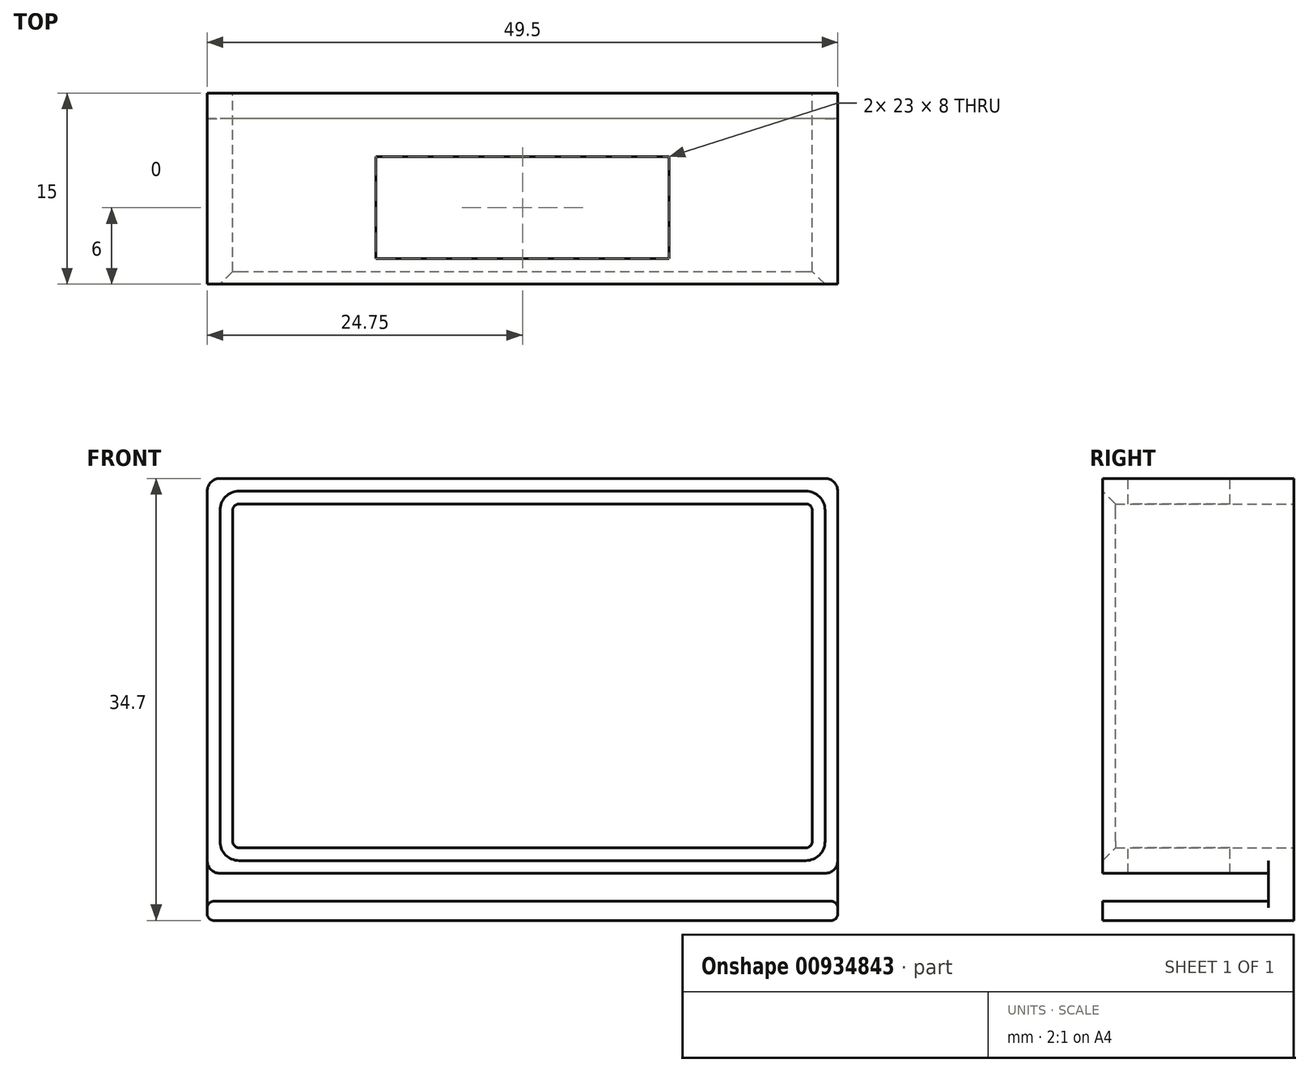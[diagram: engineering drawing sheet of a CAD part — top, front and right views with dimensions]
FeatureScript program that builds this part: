
annotation { "Feature Type Name" : "Feature", "Feature Type Description" : "" }
export const myFeature = defineFeature(function(context is Context, id is Id, definition is map)
    precondition{}
    {
        {
            var Q0;
            Q0=qCreatedBy(makeId("Front.planeOp"),FACE);
            var sketch = newSketch(context, id + "F0", { "sketchPlane" : qUnion([Q0])});
            skLineSegment(sketch, "E0.bottom", {"start": v(22.75, -13.5) * mm, "end": v(-22.75, -13.5) * mm});
            skLineSegment(sketch, "E0.top", {"start": v(22.75, 13.5) * mm, "end": v(-22.75, 13.5) * mm});
            skLineSegment(sketch, "E0.left", {"start": v(22.75, -13.5) * mm, "end": v(22.75, 13.5) * mm});
            skLineSegment(sketch, "E0.right", {"start": v(-22.75, -13.5) * mm, "end": v(-22.75, 13.5) * mm});
            skPoint(sketch, "E0.middle", {"position": v(0, 0) * mm});
            skLineSegment(sketch, "E1.bottom", {"start": v(24.75, -15.5) * mm, "end": v(-24.75, -15.5) * mm});
            skLineSegment(sketch, "E1.top", {"start": v(24.75, 15.5) * mm, "end": v(-24.75, 15.5) * mm});
            skLineSegment(sketch, "E1.left", {"start": v(24.75, -15.5) * mm, "end": v(24.75, 15.5) * mm});
            skLineSegment(sketch, "E1.right", {"start": v(-24.75, -15.5) * mm, "end": v(-24.75, 15.5) * mm});
            skLineSegment(sketch, "E2", {"start": v(22.75, -13.5) * mm, "end": v(22.75, -15.5) * mm, "construction": true});
            skLineSegment(sketch, "E3", {"start": v(22.75, -13.5) * mm, "end": v(24.75, -13.5) * mm, "construction": true});
            skSolve(sketch);
        }
        {
            var Q0;
            Q0 = qSketchRegion(id + "F0", true);
            extrude(context, id + "F1", {"entities" : qUnion([Q0]), "depth" : 15 * mm, "offsetDistance" : 25 * mm});
        }
        {
            var Q0;
            Q0=makeQuery(id+"F1.opExtrude","SWEPT_FACE",FACE,{"disambiguationData":[OSD([sQuery(id+"F0.wireOp",EDGE,"E1.top")])]});
            var sketch = newSketch(context, id + "F2", { "sketchPlane" : qUnion([Q0])});
            skLineSegment(sketch, "E4.bottom", {"start": v(11.5, -13) * mm, "end": v(-11.5, -13) * mm});
            skLineSegment(sketch, "E4.top", {"start": v(11.5, -5) * mm, "end": v(-11.5, -5) * mm});
            skLineSegment(sketch, "E4.left", {"start": v(11.5, -13) * mm, "end": v(11.5, -5) * mm});
            skLineSegment(sketch, "E4.right", {"start": v(-11.5, -13) * mm, "end": v(-11.5, -5) * mm});
            skPoint(sketch, "E4.middle", {"position": v(0, -9) * mm});
            skSolve(sketch);
        }
        {
            var Q0;
            Q0 = qSketchRegion(id + "F2", true);
            extrude(context, id + "F3", {"entities" : qUnion([Q0]), "operationType" : NewBodyOperationType.REMOVE, "endBound" : BoundingType.THROUGH_ALL, "oppositeDirection" : true, "depth" : 25 * mm, "offsetDistance" : 25 * mm});
        }
        {
            var Q0;
            Q0=makeQuery(id+"F1.opExtrude","SWEPT_EDGE",EDGE,{"disambiguationData":[OSD([sQuery(id+"F0.wireOp",EDGE,"E1.top"),sQuery(id+"F0.wireOp",EDGE,"E1.left")])]});
            var Q1;
            Q1=makeQuery(id+"F1.opExtrude","SWEPT_EDGE",EDGE,{"disambiguationData":[OSD([sQuery(id+"F0.wireOp",EDGE,"E1.bottom"),sQuery(id+"F0.wireOp",EDGE,"E1.left")])]});
            var Q2;
            Q2=makeQuery(id+"F1.opExtrude","SWEPT_EDGE",EDGE,{"disambiguationData":[OSD([sQuery(id+"F0.wireOp",EDGE,"E1.top"),sQuery(id+"F0.wireOp",EDGE,"E1.right")])]});
            var Q3;
            Q3=makeQuery(id+"F1.opExtrude","SWEPT_EDGE",EDGE,{"disambiguationData":[OSD([sQuery(id+"F0.wireOp",EDGE,"E1.bottom"),sQuery(id+"F0.wireOp",EDGE,"E1.right")])]});
            fillet(context, id + "F4", {"entities" : qUnion([Q0, Q1, Q2, Q3]), "radius" : 1 * mm, "tangentPropagation" : true, "allowEdgeOverflow" : false});
        }
        {
            var Q0;
            Q0=makeQuery(id+"F1.opExtrude","SWEPT_EDGE",EDGE,{"disambiguationData":[OSD([sQuery(id+"F0.wireOp",EDGE,"E0.top"),sQuery(id+"F0.wireOp",EDGE,"E0.right")])]});
            var Q1;
            Q1=makeQuery(id+"F1.opExtrude","SWEPT_EDGE",EDGE,{"disambiguationData":[OSD([sQuery(id+"F0.wireOp",EDGE,"E0.top"),sQuery(id+"F0.wireOp",EDGE,"E0.left")])]});
            var Q2;
            Q2=makeQuery(id+"F1.opExtrude","SWEPT_EDGE",EDGE,{"disambiguationData":[OSD([sQuery(id+"F0.wireOp",EDGE,"E0.bottom"),sQuery(id+"F0.wireOp",EDGE,"E0.left")])]});
            var Q3;
            Q3=makeQuery(id+"F1.opExtrude","SWEPT_EDGE",EDGE,{"disambiguationData":[OSD([sQuery(id+"F0.wireOp",EDGE,"E0.bottom"),sQuery(id+"F0.wireOp",EDGE,"E0.right")])]});
            fillet(context, id + "F5", {"entities" : qUnion([Q0, Q1, Q2, Q3]), "radius" : .5 * mm, "tangentPropagation" : true, "allowEdgeOverflow" : false});
        }
        {
            var Q0;
            Q0=qCreatedBy(makeId("Front.planeOp"),FACE);
            var sketch = newSketch(context, id + "F6", { "sketchPlane" : qUnion([Q0])});
            skLineSegment(sketch, "E5.bottom", {"start": v(24.75, -19.2) * mm, "end": v(-24.75, -19.2) * mm});
            skLineSegment(sketch, "E5.top", {"start": v(24.75, -17.7) * mm, "end": v(-24.75, -17.7) * mm});
            skLineSegment(sketch, "E5.left", {"start": v(24.75, -19.2) * mm, "end": v(24.75, -17.7) * mm});
            skLineSegment(sketch, "E5.right", {"start": v(-24.75, -19.2) * mm, "end": v(-24.75, -17.7) * mm});
            skPoint(sketch, "E5.middle", {"position": v(0, -18.45) * mm});
            skSolve(sketch);
        }
        {
            var Q0;
            Q0 = qSketchRegion(id + "F6", true);
            var Q1;
            Q1=makeQuery(id+"F1.opExtrude","CAP_FACE",FACE,{"disambiguationData":[OSD([sQuery(id+"F0.wireOp",EDGE,"E0.bottom"),sQuery(id+"F0.wireOp",EDGE,"E0.top"),sQuery(id+"F0.wireOp",EDGE,"E0.left"),sQuery(id+"F0.wireOp",EDGE,"E0.right"),sQuery(id+"F0.wireOp",EDGE,"E1.bottom"),sQuery(id+"F0.wireOp",EDGE,"E1.top"),sQuery(id+"F0.wireOp",EDGE,"E1.left"),sQuery(id+"F0.wireOp",EDGE,"E1.right")])],"isStart":false});
            extrude(context, id + "F7", {"entities" : qUnion([Q0]), "endBound" : BoundingType.UP_TO_SURFACE, "depth" : 25 * mm, "endBoundEntityFace" : qUnion([Q1]), "offsetDistance" : 25 * mm});
        }
        {
            var Q0;
            Q0=qCreatedBy(makeId("Front.planeOp"),FACE);
            var sketch = newSketch(context, id + "F8", { "sketchPlane" : qUnion([Q0])});
            skLineSegment(sketch, "E6.bottom", {"start": v(24.75, -19.2) * mm, "end": v(-24.75, -19.2) * mm});
            skLineSegment(sketch, "E6.top", {"start": v(24.75, -13.5) * mm, "end": v(-24.75, -13.5) * mm});
            skLineSegment(sketch, "E6.left", {"start": v(24.75, -19.2) * mm, "end": v(24.75, -13.5) * mm});
            skLineSegment(sketch, "E6.right", {"start": v(-24.75, -19.2) * mm, "end": v(-24.75, -13.5) * mm});
            skPoint(sketch, "E6.middle", {"position": v(0, -16.35) * mm});
            skSolve(sketch);
        }
        {
            var Q0;
            Q0 = qSketchRegion(id + "F8", true);
            extrude(context, id + "F9", {"entities" : qUnion([Q0]), "operationType" : NewBodyOperationType.ADD, "depth" : 2 * mm, "offsetDistance" : 25 * mm});
        }
        {
            var Q0;
            Q0=makeQuery(id+"F7.opExtrude","SWEPT_EDGE",EDGE,{"disambiguationData":[OSD([sQuery(id+"F6.wireOp",EDGE,"E5.bottom"),sQuery(id+"F6.wireOp",EDGE,"E5.left")])]});
            var Q1;
            Q1=makeQuery(id+"F7.opExtrude","SWEPT_EDGE",EDGE,{"disambiguationData":[OSD([sQuery(id+"F6.wireOp",EDGE,"E5.top"),sQuery(id+"F6.wireOp",EDGE,"E5.left")])]});
            var Q2;
            Q2=makeQuery(id+"F7.opExtrude","SWEPT_EDGE",EDGE,{"disambiguationData":[OSD([sQuery(id+"F6.wireOp",EDGE,"E5.bottom"),sQuery(id+"F6.wireOp",EDGE,"E5.right")])]});
            var Q3;
            Q3=makeQuery(id+"F7.opExtrude","SWEPT_EDGE",EDGE,{"disambiguationData":[OSD([sQuery(id+"F6.wireOp",EDGE,"E5.top"),sQuery(id+"F6.wireOp",EDGE,"E5.right")])]});
            fillet(context, id + "F10", {"entities" : qUnion([Q0, Q1, Q2, Q3]), "radius" : .5 * mm, "tangentPropagation" : true, "allowEdgeOverflow" : false});
        }
        {
            var Q0;
            Q0=makeQuery(id+"F1.opExtrude","CAP_EDGE",EDGE,{"disambiguationData":[OSD([sQuery(id+"F0.wireOp",EDGE,"E0.top")])],"isStart":false});
            chamfer(context, id + "F11", {"entities" : qUnion([Q0]), "width" : 1 * mm, "tangentPropagation" : true});
        }
    });
